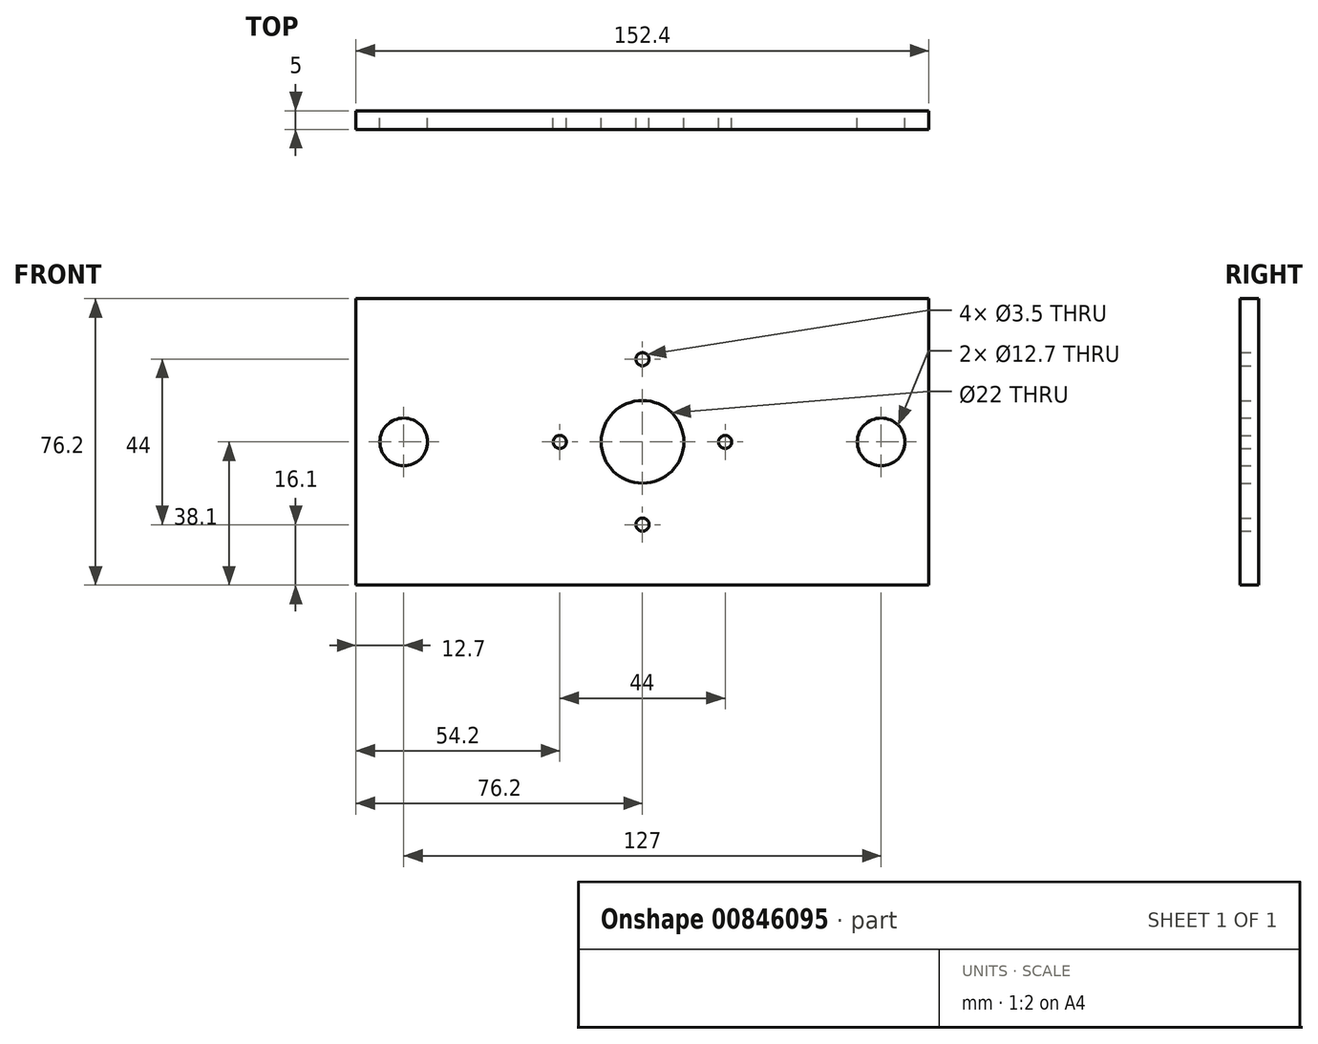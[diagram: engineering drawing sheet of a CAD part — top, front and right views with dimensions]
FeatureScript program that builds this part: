
annotation { "Feature Type Name" : "Feature", "Feature Type Description" : "" }
export const myFeature = defineFeature(function(context is Context, id is Id, definition is map)
    precondition{}
    {
        {
            var Q0;
            Q0=qCreatedBy(makeId("Front.planeOp"),FACE);
            var sketch = newSketch(context, id + "F0", { "sketchPlane" : qUnion([Q0])});
            skLineSegment(sketch, "E0.bottom", {"start": v(-76.2, -38.1) * mm, "end": v(76.2, -38.1) * mm});
            skLineSegment(sketch, "E0.top", {"start": v(-76.2, 38.1) * mm, "end": v(76.2, 38.1) * mm});
            skLineSegment(sketch, "E0.left", {"start": v(-76.2, -38.1) * mm, "end": v(-76.2, 38.1) * mm});
            skLineSegment(sketch, "E0.right", {"start": v(76.2, -38.1) * mm, "end": v(76.2, 38.1) * mm});
            skPoint(sketch, "E0.middle", {"position": v(0, 0) * mm});
            skCircle(sketch, "E1", {"center": v(-63.5, 0) * mm, "radius": 6.35 * mm});
            skCircle(sketch, "E2", {"center": v(63.5, 0) * mm, "radius": 6.35 * mm});
            skCircle(sketch, "E3", {"center": v(0, 0) * mm, "radius": 11 * mm});
            skCircle(sketch, "E4", {"center": v(-22, 0) * mm, "radius": 1.75 * mm});
            skCircle(sketch, "E5", {"center": v(0, 22) * mm, "radius": 1.75 * mm});
            skCircle(sketch, "E6", {"center": v(22, 0) * mm, "radius": 1.75 * mm});
            skCircle(sketch, "E7", {"center": v(0, -22) * mm, "radius": 1.75 * mm});
            skSolve(sketch);
        }
        {
            var Q0;
            Q0=makeQuery(id+"F0.imprint","IMPRINT",FACE,{"disambiguationData":[TD([[makeQuery(id+"F0.imprint","IMPRINT",EDGE,{"derivedFrom":sQuery(id+"F0.wireOp",EDGE,"E0.bottom")}),1.0]])]});
            extrude(context, id + "F1", {"entities" : qUnion([Q0]), "depth" : 5 * mm, "offsetDistance" : 25.4 * mm});
        }
    });
